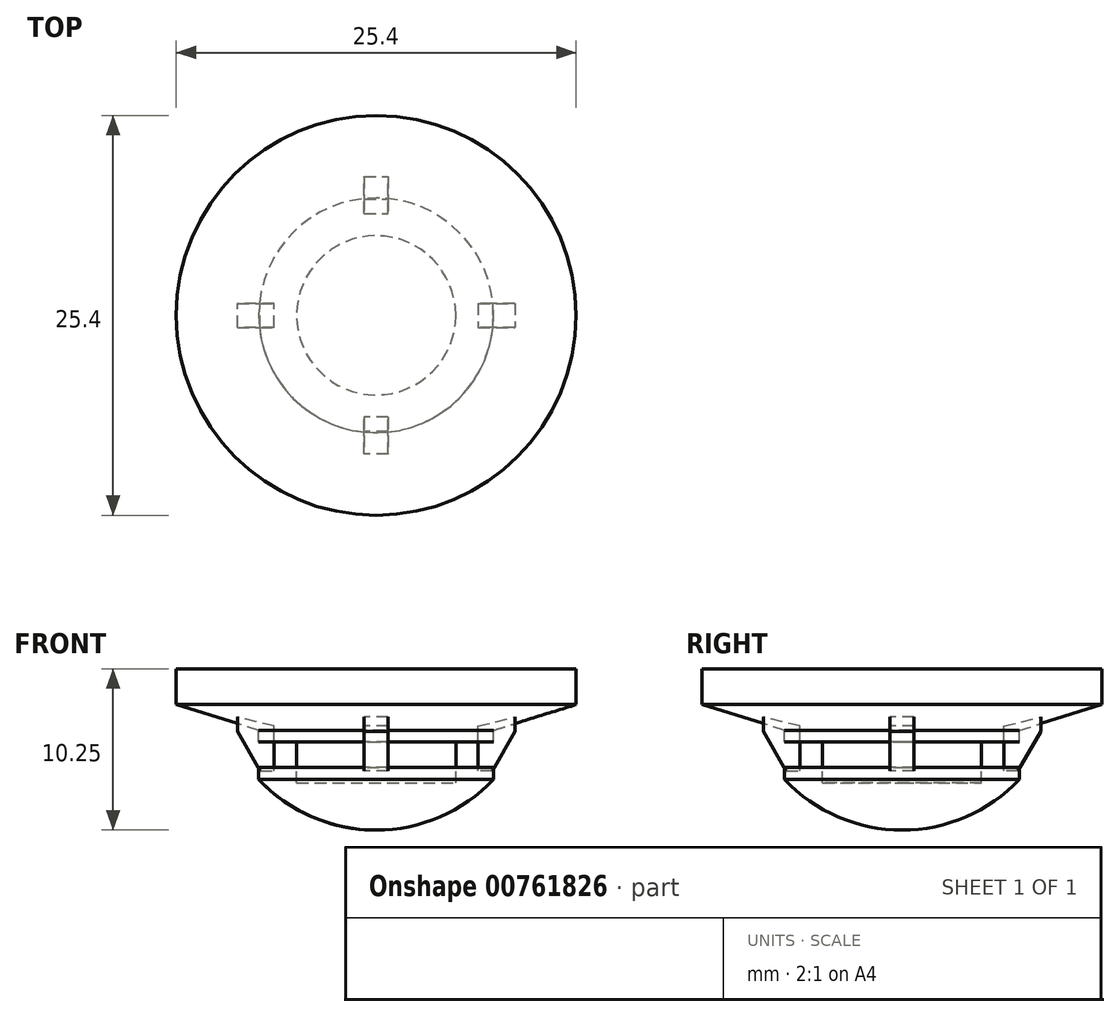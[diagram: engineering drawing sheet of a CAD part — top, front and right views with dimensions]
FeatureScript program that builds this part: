
annotation { "Feature Type Name" : "Feature", "Feature Type Description" : "" }
export const myFeature = defineFeature(function(context is Context, id is Id, definition is map)
    precondition{}
    {
        {
            var Q0;
            Q0=qCreatedBy(makeId("Front.planeOp"),FACE);
            var sketch = newSketch(context, id + "F0", { "sketchPlane" : qUnion([Q0])});
            skLineSegment(sketch, "E0", {"start": v(0, 11.67) * mm, "end": v(-12.7, 11.67) * mm});
            skLineSegment(sketch, "E1", {"start": v(-12.7, 11.67) * mm, "end": v(-12.7, 9.4) * mm});
            skLineSegment(sketch, "E2", {"start": v(-12.7, 9.4) * mm, "end": v(-7.45, 7.76) * mm});
            skLineSegment(sketch, "E3", {"start": v(-7.45, 7.76) * mm, "end": v(-7.45, 4.63) * mm});
            skArc(sketch, "E4", {"start": v(-7.45, 4.63) * mm, "mid": v(-4.06, 2.26) * mm, "end": v(0, 1.42) * mm});
            skLineSegment(sketch, "E5", {"start": v(0, 11.67) * mm, "end": v(0, 1.42) * mm});
            skSolve(sketch);
        }
        {
            var Q0;
            Q0 = qSketchRegion(id + "F0", true);
            var Q1;
            Q1=sQuery(id+"F0.wireOp",EDGE,"E5");
            revolve(context, id + "F1", {"surfaceOperationType" : NewSurfaceOperationType.NEW, "entities" : qUnion([Q0]), "axis" : qUnion([Q1]), "revolveType" : RevolveType.FULL});
        }
        {
            var Q0;
            Q0=qCreatedBy(makeId("Front.planeOp"),FACE);
            var sketch = newSketch(context, id + "F2", { "sketchPlane" : qUnion([Q0])});
            skLineSegment(sketch, "E6.bottom", {"start": v(0, 7.03) * mm, "end": v(-10.38, 7.03) * mm});
            skLineSegment(sketch, "E6.top", {"start": v(0, 5.42) * mm, "end": v(-10.38, 5.42) * mm});
            skLineSegment(sketch, "E6.left", {"start": v(0, 7.03) * mm, "end": v(0, 5.42) * mm});
            skLineSegment(sketch, "E6.right", {"start": v(-10.38, 7.03) * mm, "end": v(-10.38, 5.42) * mm});
            skSolve(sketch);
        }
        {
            var Q0;
            Q0 = qSketchRegion(id + "F2", true);
            var Q1;
            Q1=sQuery(id+"F2.wireOp",EDGE,"E6.left");
            revolve(context, id + "F3", {"operationType" : NewBodyOperationType.REMOVE, "surfaceOperationType" : NewSurfaceOperationType.NEW, "entities" : qUnion([Q0]), "axis" : qUnion([Q1]), "revolveType" : RevolveType.FULL, "oppositeDirection" : true});
        }
        {
            var Q0;
            Q0=qCreatedBy(makeId("Front.planeOp"),FACE);
            var sketch = newSketch(context, id + "F4", { "sketchPlane" : qUnion([Q0])});
            skLineSegment(sketch, "E7", {"start": v(-6.47, 8.04) * mm, "end": v(-8.81, 8.6) * mm});
            skLineSegment(sketch, "E8", {"start": v(-8.81, 8.6) * mm, "end": v(-8.81, 7.7) * mm});
            skLineSegment(sketch, "E9", {"start": v(-8.81, 7.7) * mm, "end": v(-7.37, 5.17) * mm});
            skLineSegment(sketch, "E10", {"start": v(-7.37, 5.17) * mm, "end": v(-6.47, 5.17) * mm});
            skLineSegment(sketch, "E11", {"start": v(-6.47, 5.17) * mm, "end": v(-6.47, 8.04) * mm});
            skSolve(sketch);
        }
        {
            var Q0;
            Q0 = qSketchRegion(id + "F4", true);
            extrude(context, id + "F5", {"entities" : qUnion([Q0]), "endBound" : BoundingType.SYMMETRIC, "depth" : 1.52 * mm, "offsetDistance" : 25.4 * mm});
        }
        {
            var Q0;
            Q0=qCreatedBy(makeId("Front.planeOp"),FACE);
            var sketch = newSketch(context, id + "F6", { "sketchPlane" : qUnion([Q0])});
            skLineSegment(sketch, "E12", {"start": v(0, 10.34) * mm, "end": v(0, -0.94) * mm, "construction": true});
            skSolve(sketch);
        }
        {
            var Q0;
            Q0=makeQuery(id+"F5.opExtrude","SWEPT_BODY",BODY,{"disambiguationData":[OSD([sQuery(id+"F4.wireOp",EDGE,"E7"),sQuery(id+"F4.wireOp",EDGE,"E8"),sQuery(id+"F4.wireOp",EDGE,"E9"),sQuery(id+"F4.wireOp",EDGE,"E10"),sQuery(id+"F4.wireOp",EDGE,"E11")])]});
            var Q1;
            Q1=sQuery(id+"F6.wireOp",EDGE,"E12");
            circularPattern(context, id + "F7", {"entities" : qUnion([Q0]), "axis" : qUnion([Q1]), "angle" : 360 * degree, "instanceCount" : 4, "equalSpace" : true});
        }
        {
            var Q0;
            Q0=makeQuery(id+"F3.boolean.opBoolean","COPY",FACE,{"derivedFrom":makeQuery(id+"F3.opRevolve","SWEPT_FACE",FACE,{"disambiguationData":[OSD([sQuery(id+"F2.wireOp",EDGE,"E6.bottom")])]})});
            var sketch = newSketch(context, id + "F8", { "sketchPlane" : qUnion([Q0])});
            skCircle(sketch, "E13", {"center": v(0, 0) * mm, "radius": 5.06 * mm});
            skSolve(sketch);
        }
        {
            var Q0;
            Q0 = qSketchRegion(id + "F8", true);
            extrude(context, id + "F9", {"entities" : qUnion([Q0]), "depth" : 2.62 * mm, "offsetDistance" : 25.4 * mm});
        }
    });
